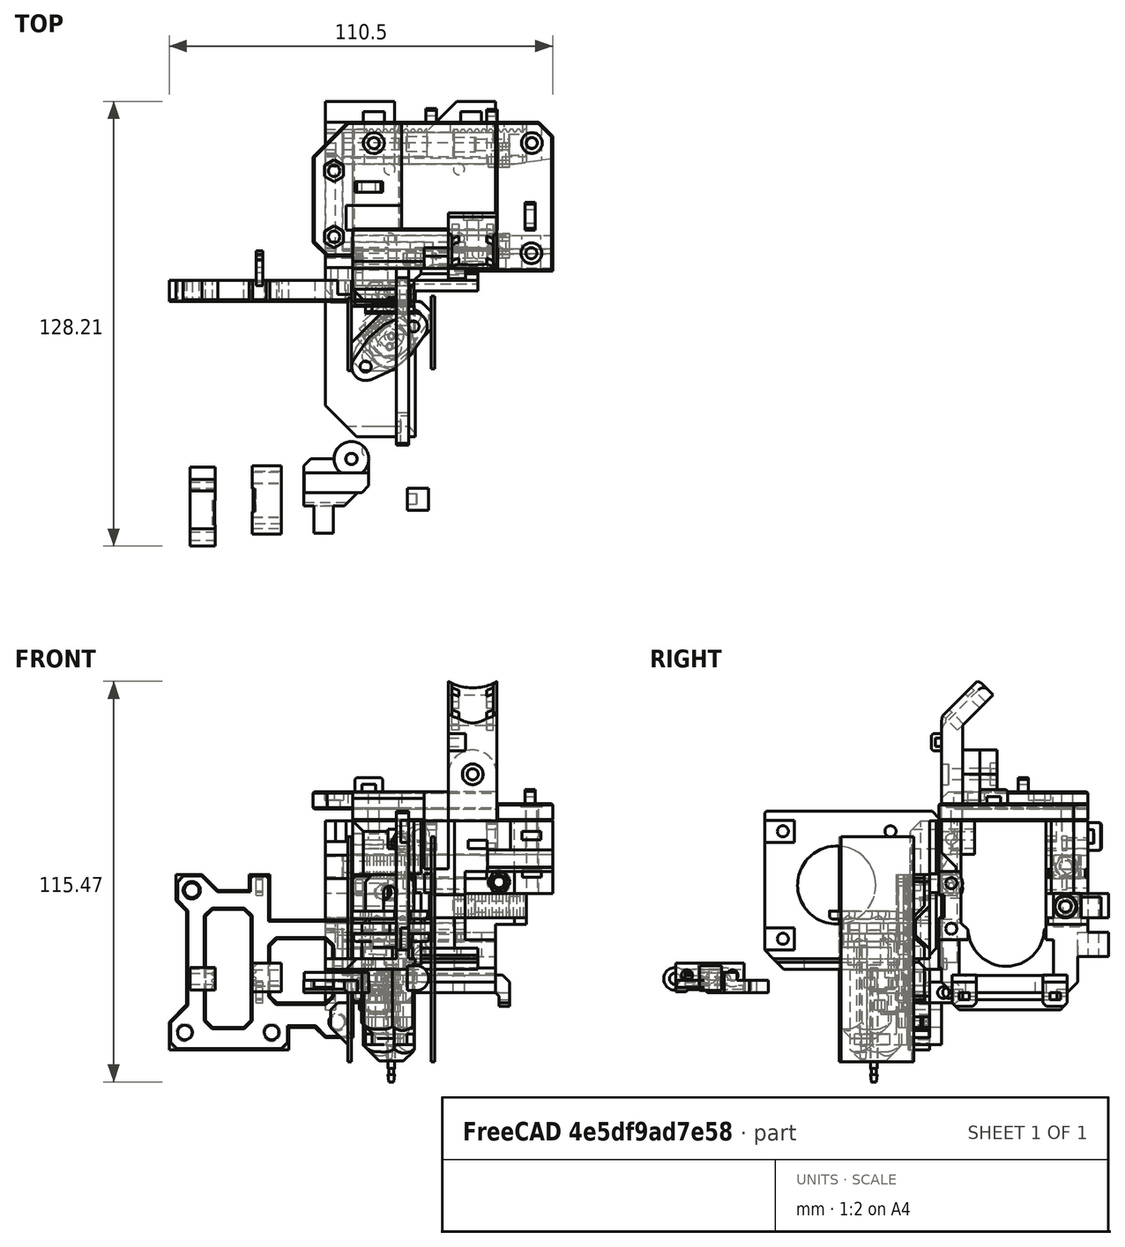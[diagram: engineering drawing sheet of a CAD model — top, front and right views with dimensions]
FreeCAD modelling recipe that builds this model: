
FCSTD DOCUMENT  (FreeCAD 0.18R16146 (Git))
Label: titan-aero-2-tmp
License: All rights reserved
LicenseURL: http://en.wikipedia.org/wiki/All_rights_reserved
objects: Part::Box×84, Part::Cut×67, Part::Cylinder×64, Part::MultiFuse×55, Part::Chamfer×46, Part::Feature×37, Mesh::Feature×3, Part::MultiCommon×2, App::DocumentObjectGroup×1
note: 355 computed .brp shape members not serialized (recipe doc carries the construction recipe); baked Part::Feature solids carry a one-line shape summary decoded from their .brp

FEATURE [Part::Feature] Part__Feature1133001001  label="X_CarriageBODY_Hemera_Body_V003"
  shape: bbox 65.55 x 51.14 x 89.74 mm, 349 faces (baked)
FEATURE [Part::Cylinder] Cylinder
  Angle = 360
  AttacherType = Attacher::AttachEngine3D
  Height = 5
  Placement = pos=(18.5,3e-15,11.4) rot=(-1,0,0;1.5708rad)
  Radius = 3.1
FEATURE [Part::Cylinder] Cylinder001
  Angle = 360
  AttacherType = Attacher::AttachEngine3D
  Height = 9.55
  Placement = pos=(18.5,-5e-15,45.5) rot=(-1,0,0;1.5708rad)
  Radius = 3.1
FEATURE [Part::Cylinder] Cylinder002
  Angle = 360
  AttacherType = Attacher::AttachEngine3D
  Height = 5.55
  Placement = pos=(52.5,-5e-15,45.4) rot=(-1,0,0;1.5708rad)
  Radius = 3.1
FEATURE [Part::Cylinder] Cylinder003
  Angle = 360
  AttacherType = Attacher::AttachEngine3D
  Height = 7
  Placement = pos=(18.5,32.2,11.4) rot=(-1,0,0;1.5708rad)
  Radius = 2.1
FEATURE [Part::Cylinder] Cylinder004
  Angle = 360
  AttacherType = Attacher::AttachEngine3D
  Height = 12.05
  Placement = pos=(18.5,30.08,45.5) rot=(-1,0,0;1.5708rad)
  Radius = 2.1
FEATURE [Part::MultiFuse] Fusion
  Shapes = -> [Cylinder004,Cylinder003,Cylinder002,Cylinder001,Cylinder,Part__Feature1133001001]
FEATURE [Part::Box] Box  label="Cube"
  AttacherType = Attacher::AttachEngine3D
  Height = 42.5
  Length = 3.5
  Placement = pos=(0,-0.25,-0.25) rot=(0,0,1;0rad)
  Width = 42.5
FEATURE [Part::Cylinder] Cylinder005
  Angle = 360
  AttacherType = Attacher::AttachEngine3D
  Height = 10
  Placement = pos=(-1.2e-15,5.5,5.5) rot=(0,1,0;1.5708rad)
  Radius = 1.6
FEATURE [Part::Cylinder] Cylinder006
  Angle = 360
  AttacherType = Attacher::AttachEngine3D
  Height = 10
  Placement = pos=(-1.2e-15,36.5,5.5) rot=(0,1,0;1.5708rad)
  Radius = 1.6
FEATURE [Part::Cylinder] Cylinder007
  Angle = 360
  AttacherType = Attacher::AttachEngine3D
  Height = 10
  Placement = pos=(-8.1e-15,5.5,36.5) rot=(0,1,0;1.5708rad)
  Radius = 1.6
FEATURE [Part::Cylinder] Cylinder008
  Angle = 360
  AttacherType = Attacher::AttachEngine3D
  Height = 10
  Placement = pos=(-8.1e-15,36.5,36.5) rot=(0,1,0;1.5708rad)
  Radius = 1.6
FEATURE [Part::Cylinder] Cylinder009
  Angle = 360
  AttacherType = Attacher::AttachEngine3D
  Height = 10
  Placement = pos=(-5e-15,21,21) rot=(0,1,0;1.5708rad)
  Radius = 11.25
FEATURE [Part::MultiFuse] Fusion001
  Shapes = -> [Cylinder005,Cylinder006,Cylinder007,Cylinder008,Cylinder009]
FEATURE [Part::Cut] Cut
  Base = -> Box
  Placement = pos=(5.5,-47.25,11) rot=(0,0,1;0rad)
  Tool = -> Fusion001
FEATURE [Part::Cylinder] Cylinder010
  Angle = 360
  AttacherType = Attacher::AttachEngine3D
  Height = 7
  Placement = pos=(19.95,-13.75,46.5) rot=(0,1,0;1.5708rad)
  Radius = 17.5
FEATURE [Part::Feature] Fusion003
  shape: bbox 65.55 x 51.14 x 89.74 mm, 359 faces (baked)
FEATURE [Part::Box] Box001  label="Cube001"
  AttacherType = Attacher::AttachEngine3D
  Height = 46
  Length = 20
  Placement = pos=(-4,-7,49.5) rot=(0,0,1;0rad)
  Width = 26
FEATURE [Part::Box] Box002  label="Cube002"
  AttacherType = Attacher::AttachEngine3D
  Height = 46
  Length = 20
  Placement = pos=(-4,-7,49.5) rot=(0,0,1;0rad)
  Width = 26
FEATURE [Part::MultiCommon] Common  label="cable-mounter-r1"
  Placement = pos=(27.52,0,0) rot=(0,0,1;0rad)
  Shapes = -> [Box001,Fusion003]
FEATURE [Part::Cut] Cut002  label="tmp1"
  Base = -> Fusion
  Tool = -> Box002
FEATURE [Part::Box] Box004  label="Cube004"
  AttacherType = Attacher::AttachEngine3D
  Height = 3
  Length = 23.53
  Placement = pos=(-8.53,-51.5,6.75) rot=(0,0,1;0rad)
  Width = 52
FEATURE [Part::Box] Box005  label="Cube005"
  AttacherType = Attacher::AttachEngine3D
  Height = 41.5
  Length = 16.02
  Placement = pos=(-0.57,-9,8) rot=(0,0,1;0rad)
  Width = 9.25
FEATURE [Part::Box] Box006  label="Cube006"
  AttacherType = Attacher::AttachEngine3D
  Height = 11.1
  Length = 12.25
  Placement = pos=(-8.53,-9,9) rot=(0,0,1;0rad)
  Width = 9.25
FEATURE [Part::Chamfer] Chamfer004
  Base = -> Cut
  Edges = 1 edges r=1: [Edge12]
  Placement = pos=(6.45,-4,-1) rot=(0,0,1;0rad)
FEATURE [Part::Box] Box008  label="Cube008"
  AttacherType = Attacher::AttachEngine3D
  Height = 9.65
  Length = 26
  Placement = pos=(31,-0.8,39.85) rot=(0,0,1;0rad)
  Width = 10.35
FEATURE [Part::Box] Box011  label="Cube011"
  AttacherType = Attacher::AttachEngine3D
  Height = 9
  Length = 3.5
  Placement = pos=(11.95,-9,43.25) rot=(0,0,1;0rad)
  Width = 9
FEATURE [Part::Box] Box012  label="Cube012"
  AttacherType = Attacher::AttachEngine3D
  Height = 3
  Length = 3
  Placement = pos=(8,-48.5,10.75) rot=(0,0,1;0rad)
  Width = 49
FEATURE [Part::Box] Box013  label="Cube013"
  AttacherType = Attacher::AttachEngine3D
  Height = 10
  Length = 26
  Placement = pos=(-3,-4,46) rot=(0,0,1;0rad)
  Width = 4
FEATURE [Part::MultiFuse] Fusion004003
  Shapes = -> [Cut002,Box008]
FEATURE [Part::Cylinder] Cylinder010003  label="Cylinder012"
  Angle = 360
  AttacherType = Attacher::AttachEngine3D
  Height = 20
  Placement = pos=(50.8591,4.3705,41) rot=(0,0,1;0rad)
  Radius = 1.6
FEATURE [Part::Box] Box014  label="Cube014"
  AttacherType = Attacher::AttachEngine3D
  Height = 2.4
  Length = 5.5
  Placement = pos=(48.11,-3,44.1) rot=(0,0,1;0rad)
  Width = 18
FEATURE [Part::Box] Box015  label="Cube015"
  AttacherType = Attacher::AttachEngine3D
  Height = 10
  Length = 10
  Placement = pos=(2,-55.5,6.75) rot=(0,0,1;0rad)
  Width = 10
FEATURE [Part::Chamfer] Chamfer006001008
  Base = -> Box015
  Edges = 1 edges r=7: [Edge12]
  Placement = pos=(-1,4,0) rot=(0,0,1;0rad)
FEATURE [Part::Feature] Chamfer006001008001  label="Chamfer006001009"
  Placement = pos=(-5,4,0) rot=(0,0,1;0rad)
  shape: bbox 10 x 10 x 10 mm, 7 faces (baked)
FEATURE [Part::MultiFuse] Fusion004006005
  Placement = pos=(6.45,0,0) rot=(0,0,1;0rad)
  Shapes = -> [Chamfer006001008001,Chamfer006001008]
FEATURE [Part::Cylinder] Cylinder010004  label="Cylinder013"
  Angle = 360
  AttacherType = Attacher::AttachEngine3D
  Height = 20
  Placement = pos=(50.8591,4.3705,42) rot=(0,0,1;0rad)
  Radius = 1.6
FEATURE [Part::Box] Box020  label="Cube020"
  AttacherType = Attacher::AttachEngine3D
  Height = 11
  Length = 21.25
  Placement = pos=(19.95,-2.05,47.1) rot=(0,0,1;0rad)
  Width = 8.05
FEATURE [Part::Cylinder] Cylinder010005  label="Cylinder014"
  Angle = 360
  AttacherType = Attacher::AttachEngine3D
  Height = 3
  Placement = pos=(50.8591,4.3705,53.5) rot=(0,0,1;0rad)
  Radius = 3
FEATURE [Part::Box] Box024  label="Cube024"
  AttacherType = Attacher::AttachEngine3D
  Height = 5
  Length = 57.57
  Placement = pos=(-0.57,-0.8,49.5) rot=(0,0,1;0rad)
  Width = 42.93
FEATURE [Part::Cylinder] Cylinder010008  label="Cylinder017"
  Angle = 360
  AttacherType = Attacher::AttachEngine3D
  Height = 20
  Placement = pos=(50.9891,36.1405,42) rot=(0,0,1;0rad)
  Radius = 1.6
FEATURE [Part::Cylinder] Cylinder010009  label="Cylinder018"
  Angle = 360
  AttacherType = Attacher::AttachEngine3D
  Height = 2
  Placement = pos=(50.9891,36.1405,53.5) rot=(0,0,1;0rad)
  Radius = 3
FEATURE [Part::Cylinder] Cylinder010010  label="Cylinder019"
  Angle = 360
  AttacherType = Attacher::AttachEngine3D
  Height = 20
  Placement = pos=(5.4515,36.1106,42) rot=(0,0,1;0rad)
  Radius = 1.6
FEATURE [Part::MultiFuse] Fusion004006007
  Shapes = -> [Cylinder010004,Cylinder010005,Cylinder010008,Cylinder010009,Cylinder010010]
FEATURE [Part::Box] Box026  label="Cube026"
  AttacherType = Attacher::AttachEngine3D
  Height = 10
  Length = 26
  Placement = pos=(-4.5,-11,48.5) rot=(0,0,1;0rad)
  Width = 11
FEATURE [Part::Box] Box027  label="Cube027"
  AttacherType = Attacher::AttachEngine3D
  Height = 10
  Length = 42.45
  Placement = pos=(-1.4,11,52.93) rot=(0,0,1;0rad)
  Width = 36
FEATURE [Part::Box] Box028  label="Cube028"
  AttacherType = Attacher::AttachEngine3D
  Height = 5
  Length = 28.3
  Placement = pos=(12.66,11,52.93) rot=(0,0,1;0rad)
  Width = 31.13
FEATURE [Part::Box] Box030  label="Cube030"
  AttacherType = Attacher::AttachEngine3D
  Height = 15
  Length = 21
  Placement = pos=(-2.5,11,57.9301) rot=(0,0,1;0rad)
  Width = 7.13
FEATURE [Part::Feature] Fusion004006005001  label="Fusion004006010"
  Placement = pos=(-6.55,0,0) rot=(0,0,1;0rad)
  shape: bbox 14 x 10 x 10 mm, 17 faces (baked)
FEATURE [Part::MultiFuse] Fusion004006005002
  Placement = pos=(3,-3,-4) rot=(0,0,1;0rad)
  Shapes = -> [Fusion004006005001,Fusion004006005]
FEATURE [Part::Feature] Fusion004006002001  label="Fusion004006005003"
  Placement = pos=(0,0,-4) rot=(0,0,1;0rad)
  shape: bbox 31 x 27.58 x 28.28 mm, 10 faces (baked)
FEATURE [Part::Box] Box031  label="Cube031"
  AttacherType = Attacher::AttachEngine3D
  Height = 5.5
  Length = 2.4
  Placement = pos=(-26.05,-15,41.54) rot=(0,0,1;0rad)
  Width = 17
FEATURE [Part::Box] Box032  label="Cube032"
  AttacherType = Attacher::AttachEngine3D
  Height = 5.5
  Length = 2.4
  Placement = pos=(-26.05,-15,27.22) rot=(0,0,1;0rad)
  Width = 17
FEATURE [Part::MultiFuse] Fusion004006005004  label="Fusion004006005005"
  Placement = pos=(35.6,-1.75,0) rot=(0,0,1;0rad)
  Shapes = -> [Box031,Box032]
FEATURE [Part::Cut] Cut024
  Base = -> Box027
  Tool = -> Box026
FEATURE [Part::Chamfer] Chamfer006001008002
  Base = -> Box024
  Edges = 1 edges r=4: [Edge7]
FEATURE [Part::Cut] Cut025
  Base = -> Chamfer006001008002
  Tool = -> Box020
FEATURE [Part::Cut] Cut026
  Base = -> Cut025
  Tool = -> Cut024
FEATURE [Part::Cut] Cut027
  Base = -> Cut026
  Tool = -> Box013
FEATURE [Part::Box] Box034  label="Cube034"
  AttacherType = Attacher::AttachEngine3D
  Height = 5
  Length = 20.52
  Placement = pos=(-0.57,0,54) rot=(0,0,1;0rad)
  Width = 11
FEATURE [Part::Box] Box035  label="Cube035"
  AttacherType = Attacher::AttachEngine3D
  Height = 5
  Length = 20.52
  Placement = pos=(6.43,6,54) rot=(0,0,1;0rad)
  Width = 5
FEATURE [Part::MultiFuse] Fusion004006005008
  Placement = pos=(0,0,-1.07) rot=(0,0,1;0rad)
  Shapes = -> [Box034,Box035]
FEATURE [Part::Box] Box036  label="Cube036"
  AttacherType = Attacher::AttachEngine3D
  Height = 6
  Length = 20
  Placement = pos=(15.45,-6.5,6.75) rot=(0,0,1;0rad)
  Width = 7
FEATURE [Part::Cylinder] Cylinder010011  label="Cylinder020"
  Angle = 360
  AttacherType = Attacher::AttachEngine3D
  Height = 5
  Placement = pos=(33.95,16,62.93) rot=(1,0,0;1.5708rad)
  Radius = 7
FEATURE [Part::Box] Box038  label="Cube038"
  AttacherType = Attacher::AttachEngine3D
  Height = 10
  Length = 14
  Placement = pos=(26.96,11,52.93) rot=(0,0,1;0rad)
  Width = 5
FEATURE [Part::Box] Box039  label="Cube039"
  AttacherType = Attacher::AttachEngine3D
  Height = 13.43
  Length = 14
  Placement = pos=(26.96,6,49.5) rot=(0,0,1;0rad)
  Width = 5
FEATURE [Part::Cylinder] Cylinder010012  label="Cylinder021"
  Angle = 360
  AttacherType = Attacher::AttachEngine3D
  Height = 5
  Placement = pos=(33.95,11,62.93) rot=(1,0,0;1.5708rad)
  Radius = 7
FEATURE [Part::Cylinder] Cylinder010013  label="Cylinder022"
  Angle = 360
  AttacherType = Attacher::AttachEngine3D
  Height = 5
  Placement = pos=(33.95,11,62.93) rot=(1,0,0;1.5708rad)
  Radius = 1.65
FEATURE [Part::MultiFuse] Fusion004006005010002
  Shapes = -> [Box039,Cylinder010012,Fusion004006005008,Cut027]
FEATURE [Part::Cut] Cut028
  Base = -> Fusion004006005010002
  Tool = -> Cylinder010013
FEATURE [Part::Cut] Cut029
  Base = -> Cut028
  Tool = -> Fusion004006007
FEATURE [Part::Chamfer] Chamfer006001008011
  Base = -> Cut029
  Edges = 1 edges r=2: [Edge125]
FEATURE [Part::Cylinder] Cylinder010014  label="Cylinder023"
  Angle = 360
  AttacherType = Attacher::AttachEngine3D
  Height = 5
  Placement = pos=(33.95,16,62.93) rot=(1,0,0;1.5708rad)
  Radius = 1.65
FEATURE [Part::Feature] Pad001
  Placement = pos=(33.96,16,62.93) rot=(1,0,0;1.5708rad)
  shape: bbox 5.543 x 2 x 6.4 mm, 8 faces (baked)
FEATURE [Part::Cylinder] Cylinder010015  label="Cylinder024"
  Angle = 360
  AttacherType = Attacher::AttachEngine3D
  Height = 10
  Placement = pos=(0,0,0) rot=(0,1,0;1.5708rad)
  Radius = 1.65
FEATURE [Part::Cylinder] Cylinder010016  label="Cylinder025"
  Angle = 360
  AttacherType = Attacher::AttachEngine3D
  Height = 10
  Placement = pos=(-6.9e-15,0,31) rot=(0,1,0;1.5708rad)
  Radius = 1.65
FEATURE [Part::Box] Box040  label="Cube040"
  AttacherType = Attacher::AttachEngine3D
  Height = 6
  Length = 1.5
  Placement = pos=(0,-3,-3) rot=(0,0,1;0rad)
  Width = 6
FEATURE [Part::Box] Box041  label="Cube041"
  AttacherType = Attacher::AttachEngine3D
  Height = 6
  Length = 1.5
  Placement = pos=(0,-3,28) rot=(0,0,1;0rad)
  Width = 6
FEATURE [Part::Box] Box042  label="Cube042"
  AttacherType = Attacher::AttachEngine3D
  Height = 6
  Length = 2
  Placement = pos=(0,-3,28) rot=(0,0,1;0rad)
  Width = 6
FEATURE [Part::Box] Box043  label="Cube043"
  AttacherType = Attacher::AttachEngine3D
  Height = 6
  Length = 2
  Placement = pos=(0,-3,-3) rot=(0,0,1;0rad)
  Width = 6
FEATURE [Part::Cylinder] Cylinder010017  label="Cylinder026"
  Angle = 360
  AttacherType = Attacher::AttachEngine3D
  Height = 10
  Placement = pos=(-6.9e-15,0,31) rot=(0,1,0;1.5708rad)
  Radius = 1.65
FEATURE [Part::Cylinder] Cylinder010018  label="Cylinder027"
  Angle = 360
  AttacherType = Attacher::AttachEngine3D
  Height = 10
  Placement = pos=(0,0,0) rot=(0,1,0;1.5708rad)
  Radius = 1.65
FEATURE [Part::MultiFuse] Fusion004006005010004
  Shapes = -> [Cylinder010018,Cylinder010017]
FEATURE [Part::MultiFuse] Fusion004006005010005
  Shapes = -> [Box042,Box043]
FEATURE [Part::Cut] Cut033
  Base = -> Fusion004006005010005
  Tool = -> Fusion004006005010004
FEATURE [Part::MultiFuse] Fusion004006005010006
  Shapes = -> [Box040,Box041]
FEATURE [Part::MultiFuse] Fusion004006005010007
  Shapes = -> [Cylinder010015,Cylinder010016]
FEATURE [Part::Cut] Cut034
  Base = -> Fusion004006005010006
  Placement = pos=(-28,0,0) rot=(0,0,1;0rad)
  Tool = -> Fusion004006005010007
FEATURE [Part::MultiFuse] Fusion004006005010008
  Shapes = -> [Cut034]
FEATURE [Part::Chamfer] Chamfer006001008014
  Base = -> Fusion004006005010008
  Edges = 4 edges r=1: [Edge9,Edge11,Edge24,Edge26]
  Placement = pos=(0,0.5,0) rot=(0,0,1;0rad)
FEATURE [Part::Chamfer] Chamfer006001008015
  Base = -> Cut033
  Edges = 4 edges r=1: [Edge9,Edge11,Edge24,Edge26]
  Placement = pos=(0.25,0.5,0) rot=(0,0,1;0rad)
FEATURE [Part::Box] Box046  label="Cube046"
  AttacherType = Attacher::AttachEngine3D
  Height = 33
  Length = 10
  Placement = pos=(-8,-11,2.5) rot=(0,0,1;0rad)
  Width = 27
FEATURE [Part::Box] Box047  label="Cube047"
  AttacherType = Attacher::AttachEngine3D
  Height = 6
  Length = 2
  Placement = pos=(0.25,-5,-3) rot=(0,0,1;0rad)
  Width = 3
FEATURE [Part::Box] Box048  label="Cube048"
  AttacherType = Attacher::AttachEngine3D
  Height = 6
  Length = 2
  Placement = pos=(0.25,-5,28) rot=(0,0,1;0rad)
  Width = 3
FEATURE [Part::Box] Box049  label="Cube049"
  AttacherType = Attacher::AttachEngine3D
  Height = 6
  Length = 1.5
  Placement = pos=(-28,-5,28) rot=(0,0,1;0rad)
  Width = 3
FEATURE [Part::Box] Box050  label="Cube050"
  AttacherType = Attacher::AttachEngine3D
  Height = 6
  Length = 1.5
  Placement = pos=(-28,-5,-3) rot=(0,0,1;0rad)
  Width = 3
FEATURE [Part::Feature] Box051001  label="Cube052"
  Placement = pos=(0,-17,19) rot=(0,0,1;0rad)
  shape: bbox 7 x 28.28 x 28.28 mm, 6 faces (baked)
FEATURE [Part::Cut] Cut035
  Base = -> Box051001
  Placement = pos=(0,6,-0.25) rot=(0,0,1;0rad)
  Tool = -> Box046
FEATURE [Part::Box] Box051002  label="Cube053"
  AttacherType = Attacher::AttachEngine3D
  Height = 10
  Length = 10
  Placement = pos=(-8,-19,11.5) rot=(0,0,1;0rad)
  Width = 10
FEATURE [Part::Cut] Cut036
  Base = -> Cut035
  Tool = -> Box051002
FEATURE [Part::Feature] Cut036001  label="Cut037"
  Placement = pos=(7,0,0) rot=(0,0,1;0rad)
  shape: bbox 7 x 4 x 12 mm, 6 faces (baked)
FEATURE [Part::Feature] Cut036002  label="Cut038"
  Placement = pos=(14,0,0) rot=(0,0,1;0rad)
  shape: bbox 7 x 4 x 12 mm, 6 faces (baked)
FEATURE [Part::Feature] Cut036003  label="Cut039"
  Placement = pos=(21,0,0) rot=(0,0,1;0rad)
  shape: bbox 7 x 4 x 12 mm, 6 faces (baked)
FEATURE [Part::MultiFuse] Fusion004006005010011
  Placement = pos=(0,0,0.25) rot=(0,0,1;0rad)
  Shapes = -> [Cut036003,Cut036001,Cut036002,Cut036]
FEATURE [Mesh::Feature] Radial_Fan_5015
  Placement = pos=(13.5,-54,24) rot=(1,0,0;1.5708rad)
FEATURE [Part::Cylinder] Cylinder010020  label="Cylinder029"
  Angle = 360
  AttacherType = Attacher::AttachEngine3D
  Height = 35
  Placement = pos=(-47,6.9e-15,29.5) rot=(1,0,0;1.5708rad)
  Radius = 2.1
FEATURE [Part::Cylinder] Cylinder010021  label="Cylinder030"
  Angle = 360
  AttacherType = Attacher::AttachEngine3D
  Height = 35
  Placement = pos=(-5,-1.1e-15,-8.5) rot=(1,0,0;1.5708rad)
  Radius = 2.1
FEATURE [Part::Cylinder] Cylinder010022  label="Cylinder031"
  Angle = 360
  AttacherType = Attacher::AttachEngine3D
  Height = 45
  Placement = pos=(10,6,29) rot=(1,0,0;1.5708rad)
  Radius = 2.1
FEATURE [Part::Cylinder] Cylinder010023  label="Cylinder032"
  Angle = 360
  AttacherType = Attacher::AttachEngine3D
  Height = 35
  Placement = pos=(-24,-1e-15,-11.5) rot=(1,0,0;1.5708rad)
  Radius = 2.1
FEATURE [Part::Cylinder] Cylinder010024  label="Cylinder033"
  Angle = 360
  AttacherType = Attacher::AttachEngine3D
  Height = 35
  Placement = pos=(-49,-1e-15,-11.5) rot=(1,0,0;1.5708rad)
  Radius = 2.1
FEATURE [Part::Box] Box051004  label="Cube055"
  AttacherType = Attacher::AttachEngine3D
  Height = 6
  Length = 1.8
  Placement = pos=(7,-11,2) rot=(0,1,0;1.5708rad)
  Width = 6
FEATURE [Part::Cylinder] Cylinder010025  label="Cylinder034"
  Angle = 360
  AttacherType = Attacher::AttachEngine3D
  Height = 27
  Placement = pos=(8,-8,6) rot=(0,1,0;3.14159rad)
  Radius = 1.65
FEATURE [Part::Box] Box051005  label="Cube056"
  AttacherType = Attacher::AttachEngine3D
  Height = 37
  Length = 6
  Placement = pos=(-1.75,-11,-3) rot=(0,0,1;0rad)
  Width = 6
FEATURE [Part::Box] Box051006  label="Cube057"
  AttacherType = Attacher::AttachEngine3D
  Height = 37
  Length = 6
  Placement = pos=(-30.5,-11,-3) rot=(0,0,1;0rad)
  Width = 6
FEATURE [Part::Box] Box051009  label="Cube060"
  AttacherType = Attacher::AttachEngine3D
  Height = 37.5
  Length = 34.5
  Placement = pos=(-53.5,-11,-16.5) rot=(0,0,1;0rad)
  Width = 6
FEATURE [Part::Box] Box051010  label="Cube061"
  AttacherType = Attacher::AttachEngine3D
  Height = 37
  Length = 13.5
  Placement = pos=(3.5,-11,-3) rot=(0,0,1;0rad)
  Width = 6
FEATURE [Part::Box] Box051011  label="Cube062"
  AttacherType = Attacher::AttachEngine3D
  Height = 34
  Length = 29
  Placement = pos=(-29.5,-11,-13) rot=(0,0,1;0rad)
  Width = 6
FEATURE [Part::Box] Box051013  label="Cube064"
  AttacherType = Attacher::AttachEngine3D
  Height = 6
  Length = 58
  Placement = pos=(-53.5,-11,-3) rot=(0,0,1;0rad)
  Width = 6
FEATURE [Part::Box] Box051014  label="Cube065"
  AttacherType = Attacher::AttachEngine3D
  Height = 13
  Length = 27
  Placement = pos=(-51.5,-11,21) rot=(0,0,1;0rad)
  Width = 6
FEATURE [Part::Box] Box051015  label="Cube066"
  AttacherType = Attacher::AttachEngine3D
  Height = 6.4
  Length = 2.2
  Placement = pos=(13.85,-48.75,16.4) rot=(0,0,1;0rad)
  Width = 9.1
FEATURE [Part::MultiFuse] Fusion004006005010014
  Shapes = -> [Box048,Box047]
FEATURE [Part::MultiFuse] Fusion004006005010015
  Shapes = -> [Box049,Box050]
FEATURE [Part::MultiFuse] Fusion004006005010016
  Shapes = -> [Chamfer006001008015,Fusion004006005010014]
FEATURE [Part::MultiFuse] Fusion004006005010017
  Shapes = -> [Chamfer006001008014,Fusion004006005010015]
FEATURE [Part::Box] Box051016  label="Cube067"
  AttacherType = Attacher::AttachEngine3D
  Height = 6.4
  Length = 2.2
  Placement = pos=(13.85,-48.75,47.4) rot=(0,0,1;0rad)
  Width = 9.1
FEATURE [Part::MultiFuse] Fusion004006005010021
  Placement = pos=(-0.6,-2.75,-4.1) rot=(0,0,1;0rad)
  Shapes = -> [Box051016,Box051015]
FEATURE [Part::Box] Box051017  label="Cube068"
  AttacherType = Attacher::AttachEngine3D
  Height = 62
  Length = 44
  Placement = pos=(-13,-61,0) rot=(0,0,1;0rad)
  Width = 10
FEATURE [Part::Feature] Fusion004006005010017001  label="Fusion004006005010022"
  Placement = pos=(-0.5,0,0) rot=(0,0,1;0rad)
  shape: bbox 1.5 x 8.5 x 37 mm, 34 faces, 2 solids (baked)
FEATURE [Part::MultiFuse] Fusion004006005010017002
  Shapes = -> [Fusion004006005010017001,Fusion004006005010017]
FEATURE [Part::Feature] Fusion004006005010017003001  label="base-mount-arm001"
  shape: bbox 30.75 x 8.5 x 37 mm, 36 faces, 4 solids (baked)
FEATURE [Part::Cylinder] Cylinder010026  label="Cylinder035"
  Angle = 360
  AttacherType = Attacher::AttachEngine3D
  Height = 27
  Placement = pos=(8,-6.6,6) rot=(0,1,0;3.14159rad)
  Radius = 0.5
FEATURE [Part::MultiFuse] Fusion004006005010017004002
  Placement = pos=(2,0,0) rot=(0,0,1;0rad)
  Shapes = -> [Cylinder010025,Cylinder010026]
FEATURE [Part::Feature] Body005001  label="Body007"
  shape: bbox 5 x 10 x 12 mm, 7 faces (baked)
FEATURE [Part::Feature] Body004001  label="Body008"
  Placement = pos=(1.5,0,8) rot=(0,0,1;0rad)
  shape: bbox 12 x 10 x 4 mm, 6 faces (baked)
FEATURE [Part::Feature] Body003001  label="Body009"
  Placement = pos=(2.5,0,9.5) rot=(0,0,1;0rad)
  shape: bbox 5 x 10 x 37 mm, 6 faces (baked)
FEATURE [Part::Feature] Body002001  label="Body010"
  Placement = pos=(4.5,0,8.5) rot=(0,0,1;0rad)
  shape: bbox 16 x 10 x 5 mm, 6 faces (baked)
FEATURE [Part::Box] Box051019  label="Cube070"
  AttacherType = Attacher::AttachEngine3D
  Height = 34
  Length = 13
  Placement = pos=(-43,-10,-10) rot=(0,0,1;0rad)
  Width = 17
FEATURE [Part::Box] Box051020  label="Cube071"
  AttacherType = Attacher::AttachEngine3D
  Height = 18.5
  Length = 18
  Placement = pos=(-24.5,-12,-3) rot=(0,0,1;0rad)
  Width = 14
FEATURE [Part::Box] Box051022  label="Cube073"
  AttacherType = Attacher::AttachEngine3D
  Height = 10
  Length = 8
  Placement = pos=(-38.5,-12,29.5) rot=(0,0,1;0rad)
  Width = 10
FEATURE [Part::Box] Box051023  label="Cube074"
  AttacherType = Attacher::AttachEngine3D
  Height = 10
  Length = 8
  Placement = pos=(-27,-11.75,-21) rot=(0,0,1;0rad)
  Width = 12
FEATURE [Part::Feature] Fusion004006005010012001  label="bltouch"
  Placement = pos=(-14.6615,56.9579,-12) rot=(0,0,-1;0.349066rad)
  shape: bbox 22.41 x 20.2 x 42.75 mm, 81 faces, 2 solids (baked)
FEATURE [Part::Cylinder] Cylinder010027  label="Cylinder036"
  Angle = 360
  AttacherType = Attacher::AttachEngine3D
  Height = 10
  Placement = pos=(-9,0,0) rot=(0,0,1;0rad)
  Radius = 1.65
FEATURE [Part::Cylinder] Cylinder010028  label="Cylinder037"
  Angle = 360
  AttacherType = Attacher::AttachEngine3D
  Height = 10
  Placement = pos=(9,0,0) rot=(0,0,1;0rad)
  Radius = 1.65
FEATURE [Part::MultiFuse] Fusion004006005010017004011  label="Fusion004006005010017004012"
  Shapes = -> [Cylinder010027,Cylinder010028]
FEATURE [Part::Cylinder] Cylinder010029  label="Cylinder038"
  Angle = 360
  AttacherType = Attacher::AttachEngine3D
  Height = 10
  Radius = 2
FEATURE [Part::Feature] Cut036009013001  label="zip-tie-mounter001"
  Placement = pos=(52.99,-16.2,49) rot=(0.57735,-0.57735,-0.57735;4.18879rad)
  shape: bbox 3 x 5 x 8 mm, 12 faces (baked)
FEATURE [Part::Feature] Cut036009013002  label="zip-tie-mounter002"
  Placement = pos=(0,10,0) rot=(0,0,1;0rad)
  shape: bbox 8 x 3 x 5 mm, 12 faces (baked)
FEATURE [Part::Feature] Cut036009013003  label="zip-tie-mounter003"
  Placement = pos=(37,19,-3.5) rot=(0,0,-1;1.5708rad)
  shape: bbox 3 x 8 x 5 mm, 12 faces (baked)
FEATURE [Part::Feature] Chamfer006001008042001  label="side-body-ziptie001"
  Placement = pos=(0,-3,0) rot=(0,0,1;0rad)
  shape: bbox 6 x 7 x 9 mm, 19 faces (baked)
FEATURE [Part::Feature] Chamfer006001008042002  label="side-body-ziptie002"
  Placement = pos=(0,23.2,0) rot=(0,0,1;0rad)
  shape: bbox 6 x 7 x 9 mm, 19 faces (baked)
FEATURE [Part::MultiFuse] Fusion004006005010017004019007  label="body-extra-mounter-r1"
  Shapes = -> [Chamfer006001008042001,Chamfer006001008042002,Cut036009013001]
FEATURE [Part::MultiFuse] Fusion004006005010017004019008
  Shapes = -> [Box038,Cylinder010011]
FEATURE [Part::MultiFuse] Fusion004006005010017004019009
  Shapes = -> [Cylinder010014,Pad001]
FEATURE [Part::Cut] Cut036009013005
  Base = -> Fusion004006005010017004019008
  Tool = -> Fusion004006005010017004019009
FEATURE [Part::Chamfer] Chamfer006001008042004
  Base = -> Cut036009013005
  Edges = 2 edges r=0.4: [Edge8,Edge16]
FEATURE [Part::Chamfer] Chamfer006001008042005
  Base = -> Box028
  Edges = 6 edges r=0.4: [Edge6,Edge8,Edge9,Edge10,Edge11,Edge12]
FEATURE [Part::Feature] Part__Feature1155001001  label="X_CarriageEndStopMount_Body002"
  shape: bbox 25.48 x 38.63 x 17 mm, 44 faces (baked)
FEATURE [Part::Cut] Cut036009013006
  Base = -> Part__Feature1155001001
  Tool = -> Box030
FEATURE [Part::Chamfer] Chamfer006001008042006
  Base = -> Cut036009013006
  Edges = 1 edges r=0.4: [Edge8]
FEATURE [Part::Chamfer] Chamfer006001008042007
  Base = -> Chamfer006001008042006
  Edges = 5 edges r=0.4: [Edge24,Edge25,Edge26,Edge27,Edge28]
FEATURE [Part::Box] Box051044  label="Cube095"
  AttacherType = Attacher::AttachEngine3D
  Height = 10
  Length = 31
  Placement = pos=(-14,0,42.9301) rot=(0,0,1;0rad)
  Width = 43
FEATURE [Part::Cut] Cut036009013007
  Base = -> Chamfer006001008042007
  Tool = -> Box051044
FEATURE [Part::Chamfer] Chamfer006001008042008
  Base = -> Cut036009013007
  Edges = 9 edges r=0.4: [Edge13,Edge14,Edge18,Edge54,Edge56,Edge57,Edge58,Edge59,Edge60]
FEATURE [Part::MultiFuse] Fusion004006005010017004019010
  Shapes = -> [Chamfer006001008042008,Cut036009013002,Chamfer006001008042004]
FEATURE [Part::MultiFuse] Fusion004006005010017004019011  label="sensor-mount-r1"
  Shapes = -> [Chamfer006001008042005,Fusion004006005010017004019010]
FEATURE [Part::Cylinder] Cylinder010033  label="Cylinder042"
  Angle = 360
  AttacherType = Attacher::AttachEngine3D
  Height = 5
  Placement = pos=(44.44,35.67,24.81) rot=(0,1,0;1.5708rad)
  Radius = 3
FEATURE [Part::Cylinder] Cylinder010034  label="Cylinder043"
  Angle = 360
  AttacherType = Attacher::AttachEngine3D
  Height = 20.85
  Placement = pos=(28.59,35.67,24.81) rot=(0,1,0;1.5708rad)
  Radius = 1.65
FEATURE [Part::Cylinder] Cylinder010035  label="Cylinder044"
  Angle = 360
  AttacherType = Attacher::AttachEngine3D
  Height = 20.85
  Placement = pos=(28.59,35.67,24.81) rot=(0,1,0;1.5708rad)
  Radius = 3.3
FEATURE [Part::Cylinder] Cylinder010036  label="inner-print-supporter-1"
  Angle = 360
  AttacherType = Attacher::AttachEngine3D
  Height = 0.2
  Placement = pos=(34.59,35.67,24.81) rot=(0,1,0;1.5708rad)
  Radius = 2.1
FEATURE [Part::Cylinder] Cylinder010037  label="Cylinder046"
  Angle = 360
  AttacherType = Attacher::AttachEngine3D
  Height = 6
  Placement = pos=(14.88,35.91,36.32) rot=(0,1,0;1.5708rad)
  Radius = 2.1
FEATURE [Part::Cylinder] Cylinder010038  label="Cylinder047"
  Angle = 360
  AttacherType = Attacher::AttachEngine3D
  Height = 29.41
  Placement = pos=(-8.53,35.91,36.32) rot=(0,1,0;1.5708rad)
  Radius = 3.3
FEATURE [Part::Cylinder] Cylinder010039  label="Cylinder048"
  Angle = 360
  AttacherType = Attacher::AttachEngine3D
  Height = 29.41
  Placement = pos=(-8.53,35.91,36.32) rot=(0,1,0;1.5708rad)
  Radius = 1.65
FEATURE [Part::Cylinder] Cylinder010040  label="inner-print-supporter-2"
  Angle = 360
  AttacherType = Attacher::AttachEngine3D
  Height = 0.2
  Placement = pos=(-3.53,35.91,36.32) rot=(0,1,0;1.5708rad)
  Radius = 3.1
FEATURE [Part::Cylinder] Cylinder010041  label="Cylinder050"
  Angle = 360
  AttacherType = Attacher::AttachEngine3D
  Height = 6.2
  Placement = pos=(28.59,35.67,24.81) rot=(0,1,0;1.5708rad)
  Radius = 2.1
FEATURE [Part::Cylinder] Cylinder010042  label="Cylinder051"
  Angle = 360
  AttacherType = Attacher::AttachEngine3D
  Height = 5.2
  Placement = pos=(-8.53,35.91,36.32) rot=(0,1,0;1.5708rad)
  Radius = 3
FEATURE [Part::Box] Box051045  label="inner-print-supporter-3"
  AttacherType = Attacher::AttachEngine3D
  Height = 10
  Length = 0.2
  Placement = pos=(28.29,32.2,19) rot=(0,0,1;0rad)
  Width = 8
FEATURE [Part::Feature] Cut036009013014  label="base-drid-plate001"
  shape: bbox 73 x 14.5 x 54 mm, 145 faces (baked)
FEATURE [Part::Box] Box051046  label="Cube097"
  AttacherType = Attacher::AttachEngine3D
  Height = 66
  Length = 54.25
  Placement = pos=(-55.25,-13,-22) rot=(0,0,1;0rad)
  Width = 26
FEATURE [Part::Box] Box051048  label="Cube099"
  AttacherType = Attacher::AttachEngine3D
  Height = 66
  Length = 54.25
  Placement = pos=(-31,-13,-69) rot=(0,0,1;0rad)
  Width = 26
FEATURE [Part::Feature] Cut036009013017001  label="grd-lite-base001"
  shape: bbox 48 x 14.5 x 54 mm, 46 faces (baked)
FEATURE [Part::Chamfer] Chamfer006001008042009
  Base = -> Cut036009013017001
  Edges = 3 edges r=2: [Edge56,Edge58,Edge60]
FEATURE [Part::Chamfer] Chamfer006001008042010
  Base = -> Chamfer006001008042009
  Edges = 3 edges r=1: [Edge28,Edge37,Edge49]
FEATURE [Part::Chamfer] Chamfer006001008042011
  Base = -> Chamfer006001008042010
  Edges = 21 edges r=0.4: [Edge1,Edge2,Edge3,Edge4,Edge5,Edge6,Edge7,Edge8,Edge9,Edge10,Edge11,Edge12,Edge13,Edge14,Edge15,Edge16,Edge17,Edge18,Edge21,Edge88,Edge89]
FEATURE [Part::Box] Box051049  label="Cube100"
  AttacherType = Attacher::AttachEngine3D
  Height = 10
  Length = 10
  Placement = pos=(-33.75,-5,-3.75) rot=(0,0,1;0rad)
  Width = 10
FEATURE [Part::MultiCommon] Common001
  Shapes = -> [Box051049,Chamfer006001008042011]
FEATURE [Part::Chamfer] Chamfer006001008042011002  label="motor-washer"
  Base = -> Common001
  Edges = 2 edges r=1: [Edge1,Edge3]
FEATURE [Part::Feature] Cut036009013017002  label="zip-tie-mounter004"
  Placement = pos=(8.5,-15.9,41) rot=(0.57735,0.57735,0.57735;4.18879rad)
  shape: bbox 3 x 5 x 8 mm, 12 faces (baked)
FEATURE [Part::Box] Box051050  label="Cube101"
  AttacherType = Attacher::AttachEngine3D
  Height = 66
  Length = 25
  Placement = pos=(-66,-13,-20) rot=(0,0,1;0rad)
  Width = 20
FEATURE [Part::Cut] Cut036009013017004
  Base = -> Cut036009013014
  Tool = -> Box051050
FEATURE [Part::Cylinder] Cylinder010043  label="Cylinder052"
  Angle = 360
  AttacherType = Attacher::AttachEngine3D
  Height = 10
  Placement = pos=(-36,-2,-15) rot=(1,0,0;1.5708rad)
  Radius = 2
FEATURE [Part::Cut] Cut036009013017005
  Base = -> Cut036009013017004
  Tool = -> Cylinder010043
FEATURE [Part::Cut] Cut036009013017006
  Base = -> Cut036009013017005
  Tool = -> Box051048
FEATURE [Part::Cut] Cut036009013017007  label="side-probe"
  Base = -> Cut036009013017006
  Tool = -> Box051046
FEATURE [Part::Feature] Cut036009013017007001  label="side-probe001"
  shape: bbox 18 x 14.5 x 37 mm, 34 faces (baked)
FEATURE [Part::Box] Box051051  label="Cube102"
  AttacherType = Attacher::AttachEngine3D
  Height = 6
  Length = 3
  Placement = pos=(-8.53,33.2,-5) rot=(0,0,1;0rad)
  Width = 3
FEATURE [Part::Box] Box051052  label="Cube103"
  AttacherType = Attacher::AttachEngine3D
  Height = 6
  Length = 3
  Placement = pos=(-8.53,3,-5) rot=(0,0,1;0rad)
  Width = 3
FEATURE [Part::Box] Box051053  label="Cube104"
  AttacherType = Attacher::AttachEngine3D
  Height = 3
  Length = 3
  Placement = pos=(-8.53,5,-5) rot=(0,0,1;0rad)
  Width = 29
FEATURE [Part::Chamfer] Chamfer006001008042011007
  Base = -> Box051051
  Edges = 1 edges r=2: [Edge11]
FEATURE [Part::Chamfer] Chamfer006001008042011008
  Base = -> Box051052
  Edges = 1 edges r=2: [Edge9]
FEATURE [Part::MultiFuse] Fusion004006005010017004019017
  Shapes = -> [Chamfer006001008042011007,Box051053,Chamfer006001008042011008]
FEATURE [Part::MultiFuse] Fusion004006005010017004019018  label="body-cable-clip"
  Shapes = -> [Fusion004006005010017004019017,Fusion004006005010017004019007,Cut036009013017002]
FEATURE [Part::Box] Box051054  label="Cube105"
  AttacherType = Attacher::AttachEngine3D
  Height = 34
  Length = 10
  Placement = pos=(-11,-10.5,21) rot=(0,0,1;0rad)
  Width = 10
FEATURE [Part::Chamfer] Chamfer006001008042011005
  Base = -> Cut036009013017007001
  Edges = 4 edges r=1: [Edge23,Edge25,Edge29,Edge43]
FEATURE [Part::Chamfer] Chamfer006001008042011006  label="probe-side-mount-r1"
  Base = -> Chamfer006001008042011005
  Edges = 13 edges r=0.4: [Edge4,Edge24,Edge31,Edge32,Edge33,Edge34,Edge35,Edge36,Edge37,Edge38,Edge39,Edge40,Edge41]
FEATURE [Mesh::Feature] titan_aero_rotate  label="titan-aero-rotate"
  Placement = pos=(35,-22,-16.5) rot=(0,0,1;3.14159rad)
FEATURE [Mesh::Feature] nema17_26mm  label="nema17-26mm"
  Placement = pos=(-14.5,-37.5,92.5) rot=(0,1,0;1.5708rad)
FEATURE [Part::Feature] Part__Feature1089001  label="X_BeltHolderRR_Hemera002"
  Placement = pos=(0,-63,-5.23) rot=(0,0,1;0rad)
  shape: bbox 18.67 x 26.47 x 5.87 mm, 22 faces (baked)
FEATURE [Part::Cylinder] Cylinder010044  label="Cylinder053"
  Angle = 360
  AttacherType = Attacher::AttachEngine3D
  Height = 3.6
  Placement = pos=(-0.99,-54.95,0) rot=(0,0,1;0rad)
  Radius = 1.65
FEATURE [Part::Cylinder] Cylinder010045  label="Cylinder054"
  Angle = 360
  AttacherType = Attacher::AttachEngine3D
  Height = 3.6
  Placement = pos=(-0.99,-54.95,0) rot=(0,0,1;0rad)
  Radius = 5
FEATURE [Part::MultiFuse] Fusion004006005010017004019020
  Shapes = -> [Part__Feature1089001,Cylinder010045]
FEATURE [Part::Cut] Cut036009013017007008  label="belt-holder-r1"
  Base = -> Fusion004006005010017004019020
  Tool = -> Cylinder010044
FEATURE [Part::Feature] Part__Feature1102001  label="belt-tesionner-r1"
  Placement = pos=(19,-65,0) rot=(0,0,1;0rad)
  shape: bbox 6.083 x 6.25 x 7.166 mm, 8 faces (baked)
FEATURE [Part::Feature] Part__Feature1088001  label="belt-holder-front-right"
  Placement = pos=(-31,-69,0) rot=(0,0,1;0rad)
  shape: bbox 8.346 x 19.65 x 8.354 mm, 38 faces (baked)
FEATURE [Part::Feature] Part__Feature1091001  label="belt-holder-front-left-r1"
  Placement = pos=(-32,-71,0) rot=(0,0,1;0rad)
  shape: bbox 7.277 x 22.78 x 6.5 mm, 35 faces (baked)
FEATURE [Part::Box] Box051055  label="Cube106"
  AttacherType = Attacher::AttachEngine3D
  Height = 10.2
  Length = 53
  Placement = pos=(-3.57,5,5) rot=(0,0,1;0rad)
  Width = 27.2
FEATURE [Part::Cylinder] Cylinder010046  label="Cylinder055"
  Angle = 360
  AttacherType = Attacher::AttachEngine3D
  Height = 18.05
  Placement = pos=(13.48,30.08,43.07) rot=(-1,0,0;1.5708rad)
  Radius = 1.6
FEATURE [Part::Cylinder] Cylinder010047  label="Cylinder056"
  Angle = 360
  AttacherType = Attacher::AttachEngine3D
  Height = 18.05
  Placement = pos=(41.49,30.08,31.84) rot=(-1,0,0;1.5708rad)
  Radius = 1.6
FEATURE [Part::Box] Box051056  label="Cube107"
  AttacherType = Attacher::AttachEngine3D
  Height = 10
  Length = 11
  Placement = pos=(35.65,28.52,18.57) rot=(0,0,1;0rad)
  Width = 16
FEATURE [Part::Cylinder] Cylinder010048  label="Cylinder057"
  Angle = 360
  AttacherType = Attacher::AttachEngine3D
  Height = 12.05
  Placement = pos=(41.49,30.08,31.84) rot=(-1,0,0;1.5708rad)
  Radius = 3.4
FEATURE [Part::Cylinder] Cylinder010049  label="Cylinder058"
  Angle = 360
  AttacherType = Attacher::AttachEngine3D
  Height = 12.05
  Placement = pos=(13.48,30.08,43.07) rot=(-1,0,0;1.5708rad)
  Radius = 3.4
FEATURE [Part::Cut] Cut036009013017007010
  Base = -> Cylinder010048
  Tool = -> Box051056
FEATURE [Part::MultiFuse] Fusion004006005010017004019022003002002
  Shapes = -> [Cut036009013017007010,Cylinder010049]
FEATURE [Part::Cylinder] Cylinder010050  label="Cylinder059"
  Angle = 360
  AttacherType = Attacher::AttachEngine3D
  Height = 6
  Placement = pos=(41.49,30.08,31.84) rot=(-1,0,0;1.5708rad)
  Radius = 2.1
FEATURE [Part::Cylinder] Cylinder010051  label="Cylinder060"
  Angle = 360
  AttacherType = Attacher::AttachEngine3D
  Height = 6
  Placement = pos=(13.48,30.08,43.07) rot=(-1,0,0;1.5708rad)
  Radius = 2.1
FEATURE [Part::MultiFuse] Fusion004006005010017004019022003002004
  Shapes = -> [Cylinder010051,Cylinder010050]
FEATURE [Part::MultiFuse] Fusion004006005010017004019022003002005
  Placement = pos=(0,-3,0) rot=(0,0,1;0rad)
  Shapes = -> [Cylinder010046,Cylinder010047]
FEATURE [Part::Box] Box051057  label="Cube108"
  AttacherType = Attacher::AttachEngine3D
  Height = 6
  Length = 16
  Placement = pos=(11.48,35,21.6) rot=(0,0,1;0rad)
  Width = 11
FEATURE [Part::Box] Box051058  label="Cube109"
  AttacherType = Attacher::AttachEngine3D
  Height = 6
  Length = 3
  Placement = pos=(20,0,28.7) rot=(0,0,1;0rad)
  Width = 5.55
FEATURE [Part::Box] Box051059  label="Cube110"
  AttacherType = Attacher::AttachEngine3D
  Height = 5.5
  Length = 2.4
  Placement = pos=(15,-1,28.781) rot=(0,0,1;0rad)
  Width = 10.55
FEATURE [Part::MultiFuse] Fusion004006005010017004019022003002006
  Shapes = -> [Fusion004003,Box051058]
FEATURE [Part::Cylinder] Cylinder010052  label="Cylinder061"
  Angle = 360
  AttacherType = Attacher::AttachEngine3D
  Height = 6
  Placement = pos=(17.4,2.77,31.53) rot=(0,1,0;1.5708rad)
  Radius = 3.25
FEATURE [Part::Cylinder] Cylinder010053  label="Cylinder062"
  Angle = 360
  AttacherType = Attacher::AttachEngine3D
  Height = 18
  Placement = pos=(14,2.77,31.53) rot=(0,1,0;1.5708rad)
  Radius = 1.6
FEATURE [Part::Box] Box051060  label="Cube111"
  AttacherType = Attacher::AttachEngine3D
  Height = 5.5
  Length = 10.4
  Placement = pos=(15,-10.54,28.781) rot=(0,0,1;0rad)
  Width = 10.55
FEATURE [Part::Cut] Cut036009013017007013
  Base = -> Cylinder010052
  Tool = -> Box051060
FEATURE [Part::MultiFuse] Fusion004006005010017004019022003002007
  Shapes = -> [Fusion004006005010017004019022003002006,Cut036009013017007013]
FEATURE [Part::MultiFuse] Fusion004006005010017004019022003002022
  Shapes = -> [Chamfer006001008011,Cut036009013003]
FEATURE [Part::Chamfer] Chamfer006001008042011014  label="top-plate-rev2"
  Base = -> Fusion004006005010017004019022003002022
  Edges = 10 edges r=0.4: [Edge51,Edge52,Edge53,Edge54,Edge55,Edge57,Edge84,Edge88,Edge89,Edge91]
FEATURE [Part::Cut] Cut036009013017007034
  Base = -> Fusion004006005010017004019022003002007
  Tool = -> Cylinder010
FEATURE [Part::Cut] Cut036009013017007035
  Base = -> Cut036009013017007034
  Tool = -> Box051059
FEATURE [Part::Cut] Cut036009013017007036
  Base = -> Cut036009013017007035
  Tool = -> Cylinder010053
FEATURE [Part::Cut] Cut036009013017007037
  Base = -> Cut036009013017007036
  Tool = -> Fusion004006002001
FEATURE [Part::Cut] Cut036009013017007038
  Base = -> Cut036009013017007037
  Tool = -> Box014
FEATURE [Part::Cut] Cut036009013017007039
  Base = -> Cut036009013017007038
  Tool = -> Cylinder010003
FEATURE [Part::MultiFuse] Fusion004006005010017004019022003002023
  Shapes = -> [Cylinder010038,Cut036009013017007039]
FEATURE [Part::MultiFuse] Fusion004006005010017004019022003002024
  Shapes = -> [Cylinder010035,Fusion004006005010017004019022003002023]
FEATURE [Part::Cut] Cut036009013017007040
  Base = -> Fusion004006005010017004019022003002024
  Tool = -> Cylinder010034
FEATURE [Part::Cut] Cut036009013017007041
  Base = -> Cut036009013017007040
  Tool = -> Cylinder010039
FEATURE [Part::Cut] Cut036009013017007042
  Base = -> Cut036009013017007041
  Tool = -> Cylinder010042
FEATURE [Part::Cut] Cut036009013017007043
  Base = -> Cut036009013017007042
  Tool = -> Cylinder010033
FEATURE [Part::Cut] Cut036009013017007044
  Base = -> Cut036009013017007043
  Tool = -> Cylinder010037
FEATURE [Part::Cut] Cut036009013017007045
  Base = -> Cut036009013017007044
  Tool = -> Cylinder010041
FEATURE [Part::Cut] Cut036009013017007046
  Base = -> Cut036009013017007045
  Tool = -> Box051057
FEATURE [Part::Cut] Cut036009013017007047
  Base = -> Cut036009013017007046
  Tool = -> Box051055
FEATURE [Part::MultiFuse] Fusion004006005010017004019022003002025
  Shapes = -> [Cut036009013017007047,Fusion004006005010017004019022003002002]
FEATURE [Part::Cut] Cut036009013017007048
  Base = -> Fusion004006005010017004019022003002025
  Tool = -> Fusion004006005010017004019022003002005
FEATURE [Part::Cut] Cut036009013017007049
  Base = -> Cut036009013017007048
  Tool = -> Fusion004006005010017004019022003002004
FEATURE [Part::MultiFuse] Fusion004006005010017004019022003002026  label="print-supporter"
  Shapes = -> [Cylinder010036,Cylinder010040,Box051045]
FEATURE [Part::MultiFuse] Fusion004006005010017004019022003002027  label="body-r2-f1"
  Shapes = -> [Cut036009013017007049,Fusion004006005010017004019018]
FEATURE [Part::Chamfer] Chamfer006001007
  Base = -> Box012
  Edges = 1 edges r=2: [Edge8]
  Placement = pos=(6.45,-3,-4) rot=(0,0,1;0rad)
FEATURE [Part::Feature] Chamfer006001007001  label="Chamfer006001008042011017"
  Placement = pos=(6.45,1,-4) rot=(0,0,1;0rad)
  shape: bbox 3.015 x 49.01 x 3.015 mm, 7 faces (baked)
FEATURE [Part::MultiFuse] Fusion004006005010017004019022003002028
  Shapes = -> [Chamfer006001007001,Chamfer006001007]
FEATURE [Part::Chamfer] Chamfer
  Base = -> Box011
  Edges = 1 edges r=2.75: [Edge12]
FEATURE [Part::Chamfer] Chamfer006001008042011017  label="Chamfer006001008042011018"
  Base = -> Box005
  Edges = 2 edges r=3: [Edge1,Edge10]
FEATURE [Part::Chamfer] Chamfer006001008042011018  label="Chamfer006001008042011019"
  Base = -> Box006
  Edges = 1 edges r=3: [Edge1]
FEATURE [Part::Box] Box051061  label="Cube112"
  AttacherType = Attacher::AttachEngine3D
  Height = 6
  Length = 20
  Placement = pos=(15.45,-10.5,9.75) rot=(0,0,1;0rad)
  Width = 7
FEATURE [Part::Cut] Cut036009013017007050
  Base = -> Box036
  Tool = -> Box051061
FEATURE [Part::Chamfer] Chamfer006001008042011019  label="Chamfer006001008042011020"
  Base = -> Cut036009013017007050
  Edges = 1 edges r=2: [Edge9]
FEATURE [Part::Chamfer] Chamfer006001008042011020  label="Chamfer006001008042011021"
  Base = -> Chamfer006001008042011019
  Edges = 1 edges r=2: [Edge18]
FEATURE [Part::Chamfer] Chamfer006001008042011021  label="Chamfer006001008042011022"
  Base = -> Box004
  Edges = 1 edges r=12: [Edge1]
FEATURE [Part::Box] Box051062  label="Cube113"
  AttacherType = Attacher::AttachEngine3D
  Height = 20
  Length = 4
  Placement = pos=(15,-3.5,8.78) rot=(0,0,1;0rad)
  Width = 8
FEATURE [Part::Box] Box051063  label="Cube114"
  AttacherType = Attacher::AttachEngine3D
  Height = 15.22
  Length = 4
  Placement = pos=(15,-3.5,34.28) rot=(0,0,1;0rad)
  Width = 8
FEATURE [Part::Chamfer] Chamfer006001008042011022  label="Chamfer006001008042011023"
  Base = -> Box051063
  Edges = 1 edges r=2: [Edge5]
FEATURE [Part::Chamfer] Chamfer006001008042011023  label="Chamfer006001008042011024"
  Base = -> Box051062
  Edges = 1 edges r=2: [Edge5]
FEATURE [Part::MultiFuse] Fusion004006005010017004019022003002029
  Shapes = -> [Chamfer006001008042011023,Chamfer006001008042011022,Chamfer006001008042011021,Chamfer006001008042011020,Chamfer006001008042011018,Chamfer006001008042011017,Chamfer,Fusion004006005010017004019022003002028,Chamfer004]
FEATURE [Part::Cut] Cut036009013017007033002
  Base = -> Fusion004006005010017004019022003002029
  Tool = -> Fusion004006005002
FEATURE [Part::Cut] Cut036009013017007033003
  Base = -> Cut036009013017007033002
  Tool = -> Fusion004006005004
FEATURE [Part::Cut] Cut036009013017007033004
  Base = -> Cut036009013017007033003
  Tool = -> Box051017
FEATURE [Part::Cut] Cut036009013017007033005  label="motor-mount-r2-f1"
  Base = -> Cut036009013017007033004
  Tool = -> Fusion004006005010021
FEATURE [App::DocumentObjectGroup] Group  label="Export"
  Group = -> [Cut036009013017007033005,Fusion004006005010017004019022003002027,Fusion004006005010017004019022003002026,Common,Chamfer006001008042011014,Cut036009013017007008,Part__Feature1102001,Part__Feature1088001,Part__Feature1091001,Fusion004006005010017004019011,Chamfer006001008042011002]
FEATURE [Part::MultiFuse] Fusion004006005010017003  label="base-mount-arm"
  Shapes = -> [Fusion004006005010017002,Fusion004006005010016]
FEATURE [Part::MultiFuse] Fusion004006005010017004019022003002032
  Shapes = -> [Cylinder010021,Cylinder010022,Cylinder010023,Cylinder010024,Cylinder010020]
FEATURE [Part::Box] Box051065  label="Cube116"
  AttacherType = Attacher::AttachEngine3D
  Height = 10
  Length = 10
  Placement = pos=(-36.5,-12,29.5) rot=(0,0,1;0rad)
  Width = 14
FEATURE [Part::Cut] Cut036009013017007033010
  Base = -> Body002001
  Tool = -> Box051065
FEATURE [Part::MultiFuse] Fusion004006005010017004019022003002033
  Shapes = -> [Box051014,Box051013,Box051011,Box051010,Box051009,Box051006,Box051005]
FEATURE [Part::MultiFuse] Fusion004006005010017004019022003002034
  Shapes = -> [Fusion004006005010017004019022003002033,Fusion004006005010017003001]
FEATURE [Part::Cut] Cut036009013017007033011
  Base = -> Fusion004006005010017004019022003002034
  Tool = -> Fusion004006005010017004019022003002032
FEATURE [Part::Cut] Cut036009013017007033018
  Base = -> Body004001
  Tool = -> Box051023
FEATURE [Part::Box] Box051066  label="Cube117"
  AttacherType = Attacher::AttachEngine3D
  Height = 10
  Length = 6
  Placement = pos=(-19,-11.75,-20) rot=(0,0,1;0rad)
  Width = 12
FEATURE [Part::Chamfer] Chamfer006001008042011029  label="Chamfer006001008042011030"
  Base = -> Box051019
  Edges = 4 edges r=2: [Edge2,Edge4,Edge6,Edge8]
FEATURE [Part::Chamfer] Chamfer006001008042011030  label="Chamfer006001008042011031"
  Base = -> Box051020
  Edges = 4 edges r=2: [Edge2,Edge4,Edge6,Edge8]
FEATURE [Part::Box] Box051067  label="Cube118"
  AttacherType = Attacher::AttachEngine3D
  Height = 49
  Length = 14
  Placement = pos=(1,-14,-14) rot=(0,0,1;0rad)
  Width = 3
FEATURE [Part::Box] Box051068  label="Cube119"
  AttacherType = Attacher::AttachEngine3D
  Height = 3
  Length = 14
  Placement = pos=(1,-26,-14) rot=(0,0,1;0rad)
  Width = 15
FEATURE [Part::Cylinder] Cylinder010056  label="Cylinder065"
  Angle = 360
  AttacherType = Attacher::AttachEngine3D
  Height = 8
  Placement = pos=(8,-20,-17) rot=(0,0,1;0rad)
  Radius = 4.15
FEATURE [Part::Cylinder] Cylinder010057  label="Cylinder066"
  Angle = 360
  AttacherType = Attacher::AttachEngine3D
  Height = 8
  Placement = pos=(8,-8,-12) rot=(0,0,1;0rad)
  Radius = 1.65
FEATURE [Part::Cylinder] Cylinder010058  label="Cylinder067"
  Angle = 360
  AttacherType = Attacher::AttachEngine3D
  Height = 10
  Placement = pos=(8,-6,30) rot=(1,0,0;1.5708rad)
  Radius = 1.7
FEATURE [Part::Cylinder] Cylinder010059  label="Cylinder068"
  Angle = 360
  AttacherType = Attacher::AttachEngine3D
  Height = 10
  Placement = pos=(8,-6,20) rot=(1,0,0;1.5708rad)
  Radius = 1.7
FEATURE [Part::Box] Box051069  label="Cube120"
  AttacherType = Attacher::AttachEngine3D
  Height = 10
  Length = 3.4
  Placement = pos=(6.3,-16,20) rot=(0,0,1;0rad)
  Width = 9
FEATURE [Part::MultiFuse] Fusion004006005010017004019022003002035
  Shapes = -> [Cylinder010058,Box051069,Cylinder010059]
FEATURE [Part::Box] Box051070  label="Cube121"
  AttacherType = Attacher::AttachEngine3D
  Height = 3
  Length = 14
  Placement = pos=(1,-14,-9) rot=(0,0,1;0rad)
  Width = 9
FEATURE [Part::Cut] Cut036009013017007033022003
  Base = -> Box051068
  Tool = -> Cylinder010056
FEATURE [Part::Chamfer] Chamfer006001008042011035
  Base = -> Cut036009013017007033022003
  Edges = 2 edges r=2: [Edge1,Edge6]
FEATURE [Part::Cut] Cut036009013017007033022005
  Base = -> Box051070
  Tool = -> Cylinder010057
FEATURE [Part::Chamfer] Chamfer006001008042011037
  Base = -> Cut036009013017007033022005
  Edges = 2 edges r=2: [Edge3,Edge12]
FEATURE [Part::Cut] Cut036009013017007033022006
  Base = -> Box051067
  Tool = -> Fusion004006005010017004019022003002035
FEATURE [Part::Chamfer] Chamfer006001008042011038
  Base = -> Cut036009013017007033022006
  Edges = 2 edges r=2: [Edge2,Edge13]
FEATURE [Part::MultiFuse] Fusion004006005010017004019022003002036  label="probe-m8-r1"
  Placement = pos=(2,1,-1) rot=(0,0,1;0rad)
  Shapes = -> [Chamfer006001008042011038,Chamfer006001008042011035,Chamfer006001008042011037]
FEATURE [Part::Box] Box051071  label="Cube122"
  AttacherType = Attacher::AttachEngine3D
  Height = 65
  Length = 1
  Placement = pos=(22,-29,-20) rot=(0,0,1;0rad)
  Width = 21
FEATURE [Part::Box] Box051072  label="Cube123"
  AttacherType = Attacher::AttachEngine3D
  Height = 65
  Length = 1
  Placement = pos=(-2,-29.5,-20) rot=(0,0,1;0rad)
  Width = 21
FEATURE [Part::Feature] Fusion004006005010012001001  label="bltouch-pref"
  Placement = pos=(0.5,3,-6.5) rot=(0,0,1;0rad)
  shape: bbox 22.41 x 20.2 x 42.75 mm, 81 faces, 2 solids (baked)
FEATURE [Part::MultiFuse] Fusion004006005010017004019022003002037  label="bltouch-hole"
  Placement = pos=(10.541,-19.5421,8) rot=(0,0,1;0.698132rad)
  Shapes = -> [Fusion004006005010017004011,Cylinder010029]
FEATURE [Part::Feature] Fusion004006005010017004019022003002037001  label="bltouch-hole001"
  Placement = pos=(0,0,9) rot=(0,0,1;0rad)
  shape: bbox 17.09 x 14.87 x 10 mm, 9 faces, 3 solids (baked)
FEATURE [Part::Box] Box051073  label="Cube124"
  AttacherType = Attacher::AttachEngine3D
  Height = 44
  Length = 14
  Placement = pos=(3,-12.5,-10) rot=(0,0,1;0rad)
  Width = 3
FEATURE [Part::Box] Box051074  label="Cube125"
  AttacherType = Attacher::AttachEngine3D
  Height = 3
  Length = 23
  Placement = pos=(-1,-29.5,17) rot=(0,0,1;0rad)
  Width = 20
FEATURE [Part::Cut] Cut036009013017007033022007
  Base = -> Box051074
  Tool = -> Fusion004006005010017004019022003002037001
FEATURE [Part::Box] Box051075  label="Cube126"
  AttacherType = Attacher::AttachEngine3D
  Height = 3
  Length = 14
  Placement = pos=(3,-12.5,-10) rot=(0,0,1;0rad)
  Width = 9
FEATURE [Part::Chamfer] Chamfer006001008042011039
  Base = -> Cut036009013017007033022007
  Edges = 1 edges r=12: [Edge3]
FEATURE [Part::Chamfer] Chamfer006001008042011040
  Base = -> Chamfer006001008042011039
  Edges = 1 edges r=12: [Edge15]
FEATURE [Part::Chamfer] Chamfer006001008042011041
  Base = -> Chamfer006001008042011040
  Edges = 2 edges r=3: [Edge12,Edge17]
FEATURE [Part::Box] Box051077  label="Cube128"
  AttacherType = Attacher::AttachEngine3D
  Height = 3
  Length = 14
  Placement = pos=(10,-12.5,14) rot=(0,0,1;0rad)
  Width = 3
FEATURE [Part::Chamfer] Chamfer006001008042011042
  Base = -> Box051077
  Edges = 1 edges r=2.5: [Edge3]
FEATURE [Part::Cut] Cut036009013017007033022008
  Base = -> Box051073
  Tool = -> Chamfer006001008042011042
FEATURE [Part::Box] Box051078  label="Cube129"
  AttacherType = Attacher::AttachEngine3D
  Height = 21
  Length = 8
  Placement = pos=(6,-12.5,-10) rot=(0,0,1;0rad)
  Width = 3
FEATURE [Part::Box] Box051079  label="Cube130"
  AttacherType = Attacher::AttachEngine3D
  Height = 3
  Length = 8
  Placement = pos=(6,-12.5,-10) rot=(0,0,1;0rad)
  Width = 3
FEATURE [Part::Cut] Cut036009013017007033022009
  Base = -> Cut036009013017007033022008
  Tool = -> Box051078
FEATURE [Part::Cut] Cut036009013017007033022010
  Base = -> Box051075
  Tool = -> Box051079
FEATURE [Part::Chamfer] Chamfer006001008042011043
  Base = -> Cut036009013017007033022009
  Edges = 1 edges r=2: [Edge12]
FEATURE [Part::Chamfer] Chamfer006001008042011044
  Base = -> Cut036009013017007033022010
  Edges = 1 edges r=2: [Edge6]
FEATURE [Part::Cylinder] Cylinder010061  label="Cylinder070"
  Angle = 360
  AttacherType = Attacher::AttachEngine3D
  Height = 20
  Placement = pos=(17.4,-13.8,-3) rot=(0,0,1;0rad)
  Radius = 3
FEATURE [Part::Cut] Cut036009013017007033022011
  Base = -> Chamfer006001008042011043
  Tool = -> Cylinder010061
FEATURE [Part::Feature] Body005002  label="Body011"
  Placement = pos=(17.4,-13.7,17) rot=(0,0,1;0rad)
  shape: bbox 6.4 x 5.543 x 6 mm, 8 faces (baked)
FEATURE [Part::Cut] Cut036009013017007033022012
  Base = -> Cut036009013017007033022011
  Tool = -> Body005002
FEATURE [Part::Chamfer] Chamfer006001008042011045
  Base = -> Cut036009013017007033022012
  Edges = 2 edges r=2: [Edge52,Edge56]
FEATURE [Part::Box] Box051080  label="Cube131"
  AttacherType = Attacher::AttachEngine3D
  Height = 8
  Length = 3.4
  Placement = pos=(8.3,-16,23) rot=(0,0,1;0rad)
  Width = 10
FEATURE [Part::Chamfer] Chamfer006001008042011046
  Base = -> Chamfer006001008042011044
  Edges = 2 edges r=2: [Edge16,Edge27]
FEATURE [Part::Cylinder] Cylinder010062  label="Cylinder071"
  Angle = 360
  AttacherType = Attacher::AttachEngine3D
  Height = 10
  Placement = pos=(10,-6,31) rot=(1,0,0;1.5708rad)
  Radius = 1.7
FEATURE [Part::Cylinder] Cylinder010063  label="Cylinder072"
  Angle = 360
  AttacherType = Attacher::AttachEngine3D
  Height = 10
  Placement = pos=(10,-6,23) rot=(1,0,0;1.5708rad)
  Radius = 1.7
FEATURE [Part::Cylinder] Cylinder010064  label="Cylinder073"
  Angle = 360
  AttacherType = Attacher::AttachEngine3D
  Height = 10
  Placement = pos=(10,-6.5,-12) rot=(0,0,1;0rad)
  Radius = 1.65
FEATURE [Part::Cut] Cut036009013017007033022014
  Base = -> Chamfer006001008042011046
  Tool = -> Cylinder010064
FEATURE [Part::MultiFuse] Fusion004006005010017004019022003002037002
  Shapes = -> [Cylinder010063,Box051080,Cylinder010062]
FEATURE [Part::Cut] Cut036009013017007033022015
  Base = -> Chamfer006001008042011045
  Tool = -> Fusion004006005010017004019022003002037002
FEATURE [Part::MultiFuse] Fusion004006005010017004019022003002037003  label="probe-bltouch-r1"
  Shapes = -> [Cut036009013017007033022015,Chamfer006001008042011041,Cut036009013017007033022014]
FEATURE [Part::Feature] Fusion004006005010011001  label="Fusion004006005010017004019022003002037003"
  Placement = pos=(0,0,-0.25) rot=(0,0,1;0rad)
  shape: bbox 28 x 4 x 12 mm, 18 faces (baked)
FEATURE [Part::MultiFuse] Fusion004006005010017004019022003002037004
  Shapes = -> [Fusion004006005010011001,Fusion004006005010011]
FEATURE [Part::MultiFuse] Fusion004006005010017004019022003002037005
  Shapes = -> [Box051004,Fusion004006005010017004002]
FEATURE [Part::Cut] Cut036009013017007033022016
  Base = -> Cut036009013017007033011
  Tool = -> Fusion004006005010017004019022003002037005
FEATURE [Part::Cut] Cut036009013017007033022017
  Base = -> Cut036009013017007033022016
  Placement = pos=(0,1.5,0) rot=(0,0,1;0rad)
  Tool = -> Fusion004006005010017004019022003002037004
FEATURE [Part::Cut] Cut036009013017007033022018
  Base = -> Cut036009013017007033022017
  Tool = -> Cut036009013017007033018
FEATURE [Part::Cut] Cut036009013017007033022019
  Base = -> Cut036009013017007033022018
  Tool = -> Box051066
FEATURE [Part::Cut] Cut036009013017007033022020
  Base = -> Cut036009013017007033022019
  Tool = -> Chamfer006001008042011029
FEATURE [Part::Cut] Cut036009013017007033022021
  Base = -> Cut036009013017007033022020
  Tool = -> Chamfer006001008042011030
FEATURE [Part::Cut] Cut036009013017007033022022
  Base = -> Cut036009013017007033022021
  Tool = -> Cut036009013017007033010
FEATURE [Part::Cut] Cut036009013017007033022023
  Base = -> Cut036009013017007033022022
  Tool = -> Box051022
FEATURE [Part::Cut] Cut036009013017007033022024
  Base = -> Cut036009013017007033022023
  Tool = -> Box051054
FEATURE [Part::Cut] Cut036009013017007033022025  label="grid-base"
  Base = -> Cut036009013017007033022024
  Tool = -> Body003001
FEATURE [Part::Feature] Cut036009013017007033022025001  label="grid-base001"
  shape: bbox 70.5 x 14.5 x 50.5 mm, 88 faces (baked)
FEATURE [Part::Chamfer] Chamfer006001008042011047
  Base = -> Cut036009013017007033022025001
  Edges = 6 edges r=2: [Edge2,Edge22,Edge24,Edge71,Edge74,Edge80]
FEATURE [Part::Chamfer] Chamfer006001008042011048
  Base = -> Chamfer006001008042011047
  Edges = 3 edges r=1: [Edge128,Edge130,Edge141]
FEATURE [Part::Chamfer] Chamfer006001008042011049
  Base = -> Chamfer006001008042011048
  Edges = 54 edges r=0.4: [Edge1,Edge2,Edge3,Edge4,Edge5,Edge6,Edge7,Edge8,Edge9,Edge10,Edge11,Edge12,Edge13,Edge14,Edge15,Edge16,Edge17,Edge18,Edge19,Edge20,Edge21,Edge22,Edge23,Edge24,Edge25,Edge26,Edge27,Edge28,Edge29,Edge30,Edge31,Edge32,Edge33,Edge34,Edge35,Edge36,Edge37,Edge38,Edge39,Edge40,Edge41,Edge42,Edge43,Edge44,+10 more]
FEATURE [Part::Chamfer] Chamfer006001008042011050  label="grid-r2-f2"
  Base = -> Chamfer006001008042011049
  Edges = 4 edges r=0.4: [Edge122,Edge123,Edge124,Edge126]
